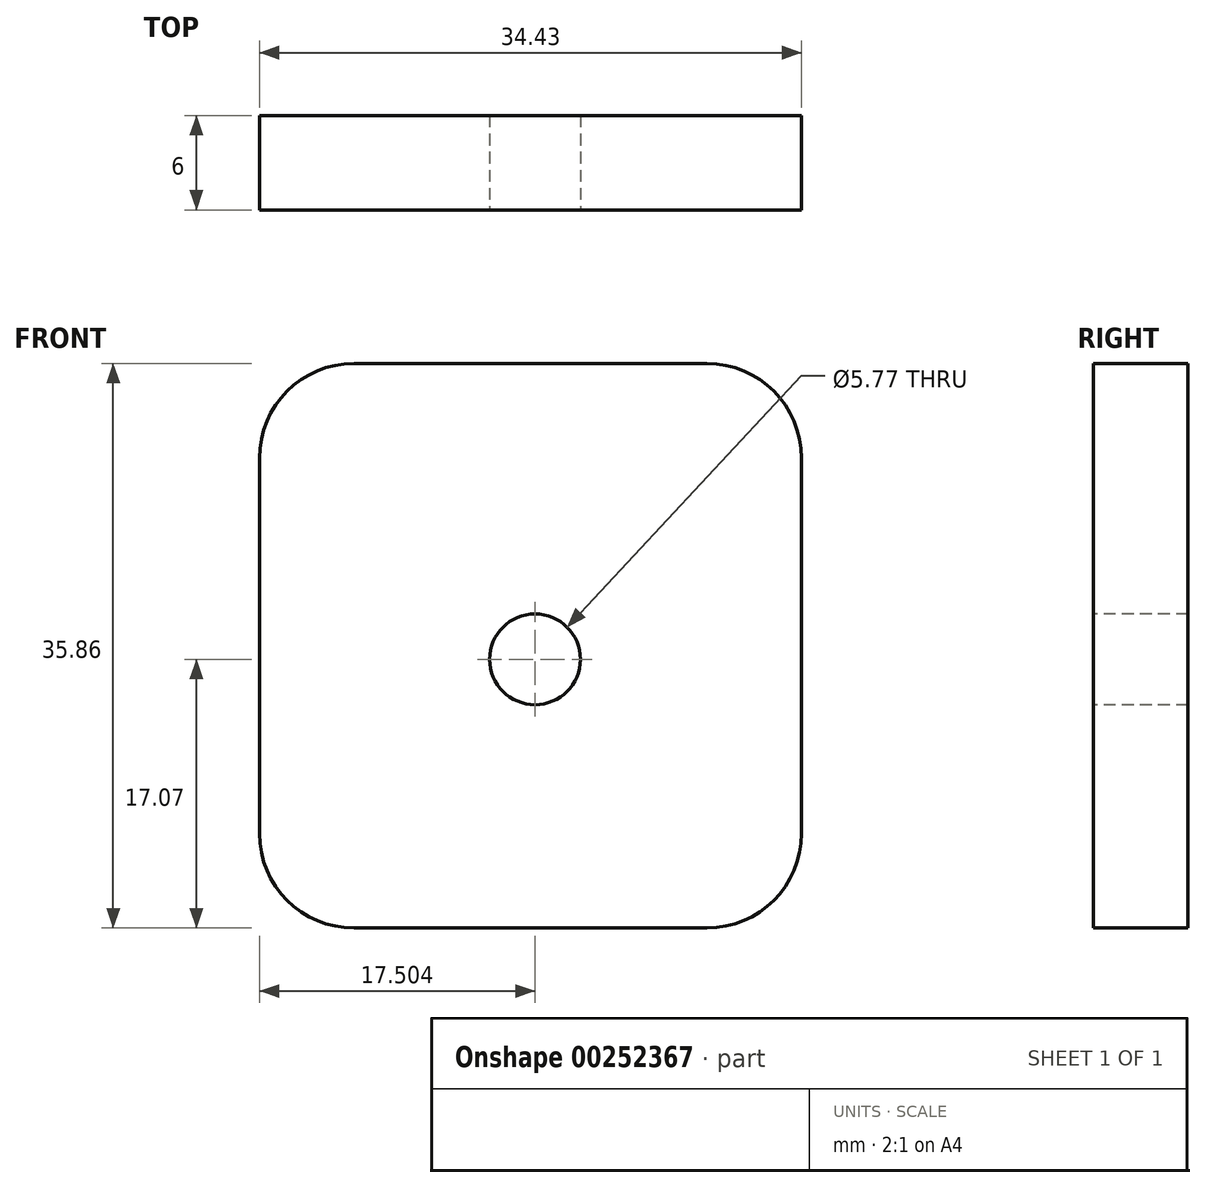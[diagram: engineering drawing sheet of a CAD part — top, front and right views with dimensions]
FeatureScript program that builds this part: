
annotation { "Feature Type Name" : "Feature", "Feature Type Description" : "" }
export const myFeature = defineFeature(function(context is Context, id is Id, definition is map)
    precondition{}
    {
        {
            var Q0;
            Q0=qCreatedBy(makeId("Front.planeOp"),FACE);
            var sketch = newSketch(context, id + "F0", { "sketchPlane" : qUnion([Q0])});
            skLineSegment(sketch, "E0.bottom", {"start": v(-6, 0) * mm, "end": v(-28.43, 0) * mm});
            skLineSegment(sketch, "E0.top", {"start": v(-6, 35.86) * mm, "end": v(-28.43, 35.86) * mm});
            skLineSegment(sketch, "E0.left", {"start": v(0, 6) * mm, "end": v(0, 29.86) * mm});
            skLineSegment(sketch, "E0.right", {"start": v(-34.43, 6) * mm, "end": v(-34.43, 29.86) * mm});
            skPoint(sketch, "E0.middle", {"position": v(-17.21, 17.93) * mm});
            skPoint(sketch, "E1.visualSharp", {"position": v(-34.43, 35.86) * mm});
            skArc(sketch, "E1.filletArc", {"start": v(-28.43, 35.86) * mm, "mid": v(-32.67, 34.1) * mm, "end": v(-34.43, 29.86) * mm});
            skPoint(sketch, "E2.visualSharp", {"position": v(0, 35.86) * mm});
            skArc(sketch, "E2.filletArc", {"start": v(0, 29.86) * mm, "mid": v(-1.76, 34.1) * mm, "end": v(-6, 35.86) * mm});
            skPoint(sketch, "E3.visualSharp", {"position": v(0, 0) * mm});
            skArc(sketch, "E3.filletArc", {"start": v(-6, 0) * mm, "mid": v(-1.76, 1.76) * mm, "end": v(0, 6) * mm});
            skPoint(sketch, "E4.visualSharp", {"position": v(-34.43, 0) * mm});
            skArc(sketch, "E4.filletArc", {"start": v(-34.43, 6) * mm, "mid": v(-32.67, 1.76) * mm, "end": v(-28.43, 0) * mm});
            skSolve(sketch);
        }
        {
            var Q0;
            Q0=makeQuery(id+"F0.imprint","IMPRINT",FACE,{"disambiguationData":[TD([[makeQuery(id+"F0.imprint","IMPRINT",EDGE,{"derivedFrom":sQuery(id+"F0.wireOp",EDGE,"E0.bottom")}),-1.0]])]});
            extrude(context, id + "F1", {"entities" : qUnion([Q0]), "depth" : 6 * mm});
        }
        {
            var Q0;
            Q0=makeQuery(id+"F1.opExtrude","CAP_FACE",FACE,{"disambiguationData":[OSD([sQuery(id+"F0.wireOp",EDGE,"E0.bottom"),sQuery(id+"F0.wireOp",EDGE,"E0.top"),sQuery(id+"F0.wireOp",EDGE,"E0.left"),sQuery(id+"F0.wireOp",EDGE,"E0.right"),sQuery(id+"F0.wireOp",EDGE,"E1.filletArc"),sQuery(id+"F0.wireOp",EDGE,"E2.filletArc"),sQuery(id+"F0.wireOp",EDGE,"E3.filletArc"),sQuery(id+"F0.wireOp",EDGE,"E4.filletArc")])],"isStart":false});
            var sketch = newSketch(context, id + "F2", { "sketchPlane" : qUnion([Q0])});
            skCircle(sketch, "E5", {"center": v(-16.93, 17.07) * mm, "radius": 2.88 * mm});
            skSolve(sketch);
        }
        {
            var Q0;
            Q0=makeQuery(id+"F2.imprint","IMPRINT",FACE,{"disambiguationData":[TD([[makeQuery(id+"F2.imprint","IMPRINT",EDGE,{"derivedFrom":sQuery(id+"F2.wireOp",EDGE,"E5")}),1.0]])]});
            extrude(context, id + "F3", {"entities" : qUnion([Q0]), "operationType" : NewBodyOperationType.REMOVE, "oppositeDirection" : true, "depth" : 30 * mm});
        }
    });
